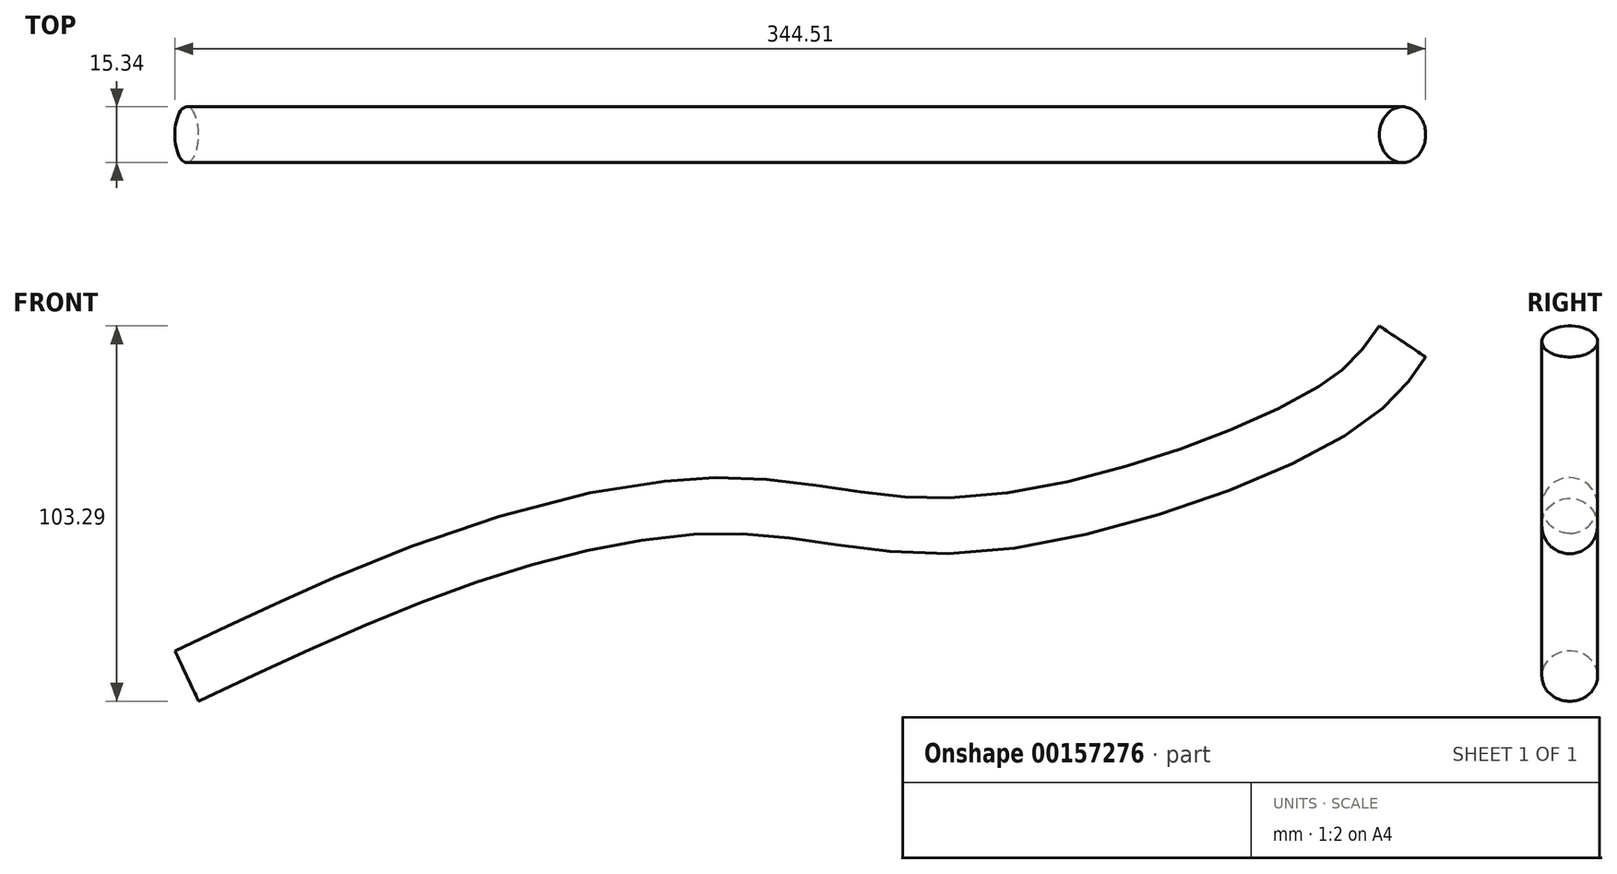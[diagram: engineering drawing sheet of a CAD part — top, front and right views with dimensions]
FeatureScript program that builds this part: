
annotation { "Feature Type Name" : "Feature", "Feature Type Description" : "" }
export const myFeature = defineFeature(function(context is Context, id is Id, definition is map)
    precondition{}
    {
        {
            var Q0;
            Q0=qCreatedBy(makeId("Front.planeOp"),FACE);
            var sketch = newSketch(context, id + "F0", { "sketchPlane" : qUnion([Q0])});
            skFitSpline(sketch, "E0", {"points": [v(-158.1, -23.6) * mm, v(-77.37, 10.62) * mm, v(-4.4, 23.23) * mm, v(59.75, 18.13) * mm, v(158.8, 50.25) * mm, v(176.77, 68.48) * mm], "startDerivative": vector(352.85, 166.59) * mm, "endDerivative": vector(95.75, 142.67) * mm});
            skSolve(sketch);
        }
        {
            var Q0;
            Q0=sQuery(id+"F0.wireOp",EDGE,"E0");
            var Q1;
            Q1=sQuery(id+"F0.wireOp",VERTEX,"E0.end");
            cPlane(context, id + "F1", {"entities" : qUnion([Q0, Q1]), "cplaneType" : CPlaneType.CURVE_POINT, "offset" : 25.4 * mm, "width" : 152.4 * mm, "height" : 152.4 * mm});
        }
        {
            var Q0;
            Q0=qCreatedBy(id+"F1.planeOp",FACE);
            var sketch = newSketch(context, id + "F2", { "sketchPlane" : qUnion([Q0])});
            skCircle(sketch, "E1", {"center": v(108.62, 0) * mm, "radius": 7.67 * mm});
            skSolve(sketch);
        }
        {
            var Q0;
            Q0=makeQuery(id+"F2.imprint","IMPRINT",FACE,{"disambiguationData":[TD([[makeQuery(id+"F2.imprint","IMPRINT",EDGE,{"derivedFrom":sQuery(id+"F2.wireOp",EDGE,"E1")}),1.0]])]});
            var Q1;
            Q1=sQuery(id+"F0.wireOp",EDGE,"E0");
            sweep(context, id + "F3", {"profiles" : qUnion([Q0]), "path" : qUnion([Q1])});
        }
    });
